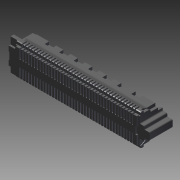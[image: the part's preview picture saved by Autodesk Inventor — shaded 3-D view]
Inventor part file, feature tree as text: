
AUTODESK INVENTOR PART (.ipt)
format: ipt  version: 2016 (Build 200138000, 138)  size: 1,748,480 bytes
history: native  units: mm
features: extrude x21, sketch x21, other x14
ambient origin geometry x8: Origin, YZ Plane, XZ Plane, XY Plane, X Axis, Y Axis, Z Axis, Center Point
bodies: Solid1 (feature_tree)
feature tree (56):
  extrude  "Extrusion1"  Depth=4.35mm TaperAngle=0.0deg
  extrude  "Extrusion2"  Depth=2.48mm TaperAngle=0.0deg
  extrude  "Extrusion3"  Depth=16.34mm TaperAngle=0.0deg
  extrude  "Extrusion4"  Depth=8.73mm TaperAngle=0.0deg
  extrude  "Extrusion5"  Depth=1.7mm TaperAngle=0.0deg
  extrude  "Extrusion6"  Depth=1.7mm TaperAngle=0.0deg
  extrude  "Extrusion7"  Depth=0.45mm TaperAngle=0.0deg
  extrude  "Extrusion8"  Depth=0.5mm TaperAngle=0.0deg
  extrude  "Extrusion9"  Depth=0.6mm TaperAngle=0.0deg
  extrude  "Extrusion10"  Depth=0.6mm TaperAngle=0.0deg
  extrude  "Extrusion11"  [1 undecoded]
  extrude  "Extrusion12"  [1 undecoded]
  extrude  "Extrusion13"  [1 undecoded]
  extrude  "Extrusion14"  [1 undecoded]
  extrude  "Extrusion15"  [1 undecoded]
  extrude  "Extrusion16"  [1 undecoded]
  extrude  "Extrusion17"  [1 undecoded]
  extrude  "Extrusion18"  [1 undecoded]
  extrude  "Extrusion19"  [1 undecoded]
  extrude  "Extrusion20"  [1 undecoded]
  extrude  "Extrusion21"  [1 undecoded]
  other  "socket_to_dummy_XY"
  other  "socket_to_dummy_YZ"
  other  "socket_to_dummy_ZX"
  other  "socket_to_dummy_X"
  other  "socket_to_dummy_Y"
  other  "socket_to_dummy_Z"
  other  "socket_to_dummy_Center"
  other  "socket_to_pad_XY"
  other  "socket_to_pad_YZ"
  other  "socket_to_pad_ZX"
  other  "socket_to_pad_X"
  other  "socket_to_pad_Y"
  other  "socket_to_pad_Z"
  other  "socket_to_pad_Center"
  sketch  "Sketch_1"  dims[d0=2.725mm d1=0.0mm d2=4.35mm d3=0.0mm]
  sketch  "Sketch_5"  dims[d4=3.0mm d5=0.0mm d6=2.48mm d7=0.0mm]
  sketch  "Sketch_6"  dims[d8=0.4mm d9=0.0mm d10=16.34mm d11=0.0mm]
  sketch  "Sketch_7"  dims[d12=3.18mm d13=0.0mm d14=8.73mm d15=0.0mm]
  sketch  "Sketch_9"  dims[d16=4.35mm d17=0.0mm d18=1.7mm d19=0.0mm]
  sketch  "Sketch_11"  dims[d20=1.7mm d21=0.0mm d22=23.54mm d23=0.0mm]
  sketch  "Sketch_12"  dims[d24=23.54mm d25=0.0mm d26=0.45mm d27=0.0mm]
  sketch  "Sketch_14"  dims[d28=0.5mm d29=0.0mm d30=0.5mm d31=0.0mm]
  sketch  "Sketch_16"  dims[d32=0.6mm d33=0.0mm d34=0.6mm d35=0.0mm]
  sketch  "Sketch_18"  dims[d36=0.6mm d37=0.0mm d38=0.6mm d39=0.0mm]
  sketch  "Sketch_19"  dims[d40=0.1mm d41=0.0mm]
  sketch  "Sketch_20"
  sketch  "Sketch_21"
  sketch  "Sketch_22"
  sketch  "Sketch_23"
  sketch  "Sketch_24"
  sketch  "Sketch_25"
  sketch  "Sketch_26"
  sketch  "Sketch_27"
  sketch  "Sketch_28"
  sketch  "Sketch_29"
note: 11 required parameter values undecoded (feature->parameter linkage not recoverable at this tier; creation-order binding heuristic only, values carry confidence <= 0.55)
